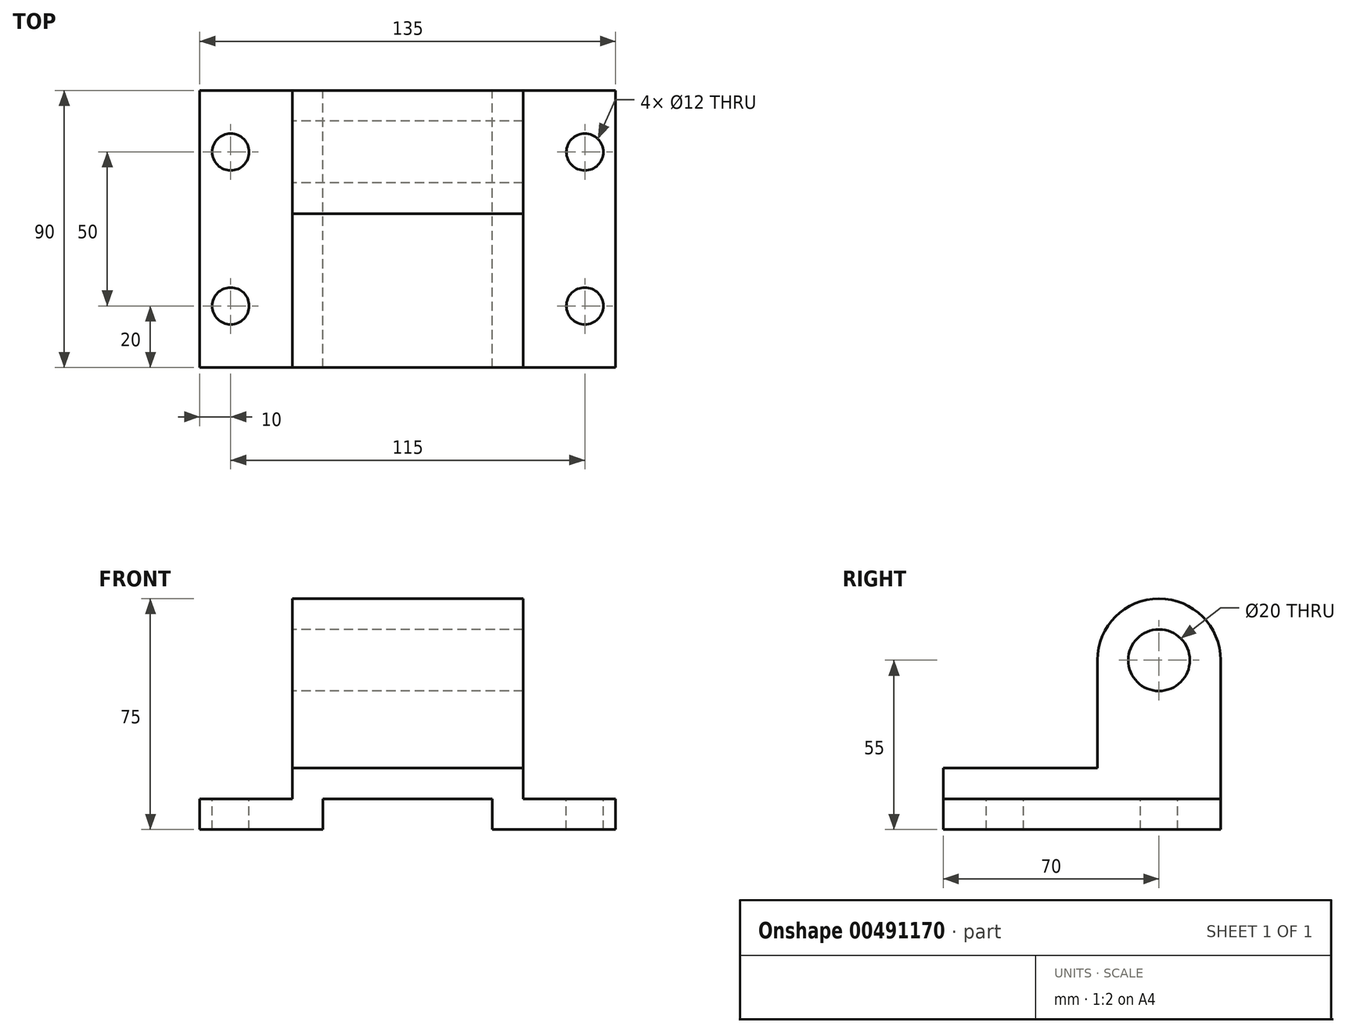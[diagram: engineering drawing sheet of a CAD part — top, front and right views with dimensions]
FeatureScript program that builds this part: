
annotation { "Feature Type Name" : "Feature", "Feature Type Description" : "" }
export const myFeature = defineFeature(function(context is Context, id is Id, definition is map)
    precondition{}
    {
        {
            var Q0;
            Q0=qCreatedBy(makeId("Front.planeOp"),FACE);
            var sketch = newSketch(context, id + "F0", { "sketchPlane" : qUnion([Q0])});
            skLineSegment(sketch, "E0", {"start": v(-95, 0) * mm, "end": v(-55, 0) * mm});
            skLineSegment(sketch, "E1", {"start": v(-55, 0) * mm, "end": v(-55, 10) * mm});
            skLineSegment(sketch, "E2", {"start": v(-55, 10) * mm, "end": v(0, 10) * mm});
            skLineSegment(sketch, "E3", {"start": v(0, 10) * mm, "end": v(0, 0) * mm});
            skLineSegment(sketch, "E4", {"start": v(0, 0) * mm, "end": v(40, 0) * mm});
            skLineSegment(sketch, "E5", {"start": v(40, 0) * mm, "end": v(40, 10) * mm});
            skLineSegment(sketch, "E6", {"start": v(40, 10) * mm, "end": v(10, 10) * mm});
            skLineSegment(sketch, "E7", {"start": v(10, 10) * mm, "end": v(10, 20) * mm});
            skLineSegment(sketch, "E8", {"start": v(10, 20) * mm, "end": v(-65, 20) * mm});
            skLineSegment(sketch, "E9", {"start": v(-65, 20) * mm, "end": v(-65, 10) * mm});
            skLineSegment(sketch, "E10", {"start": v(-65, 10) * mm, "end": v(-95, 10) * mm});
            skLineSegment(sketch, "E11", {"start": v(-95, 10) * mm, "end": v(-95, 0) * mm});
            skSolve(sketch);
        }
        {
            var Q0;
            Q0=makeQuery(id+"F0.imprint","IMPRINT",FACE,{"disambiguationData":[TD([[makeQuery(id+"F0.imprint","IMPRINT",EDGE,{"derivedFrom":sQuery(id+"F0.wireOp",EDGE,"E0")}),1.0]])]});
            extrude(context, id + "F1", {"entities" : qUnion([Q0]), "depth" : 90 * mm});
        }
        {
            var Q0;
            Q0=makeQuery(id+"F1.opExtrude","SWEPT_FACE",FACE,{"disambiguationData":[OSD([sQuery(id+"F0.wireOp",EDGE,"E10")])]});
            var sketch = newSketch(context, id + "F2", { "sketchPlane" : qUnion([Q0])});
            skCircle(sketch, "E12", {"center": v(-85, -70) * mm, "radius": 6 * mm});
            skSolve(sketch);
        }
        {
            var Q0;
            Q0=makeQuery(id+"F2.imprint","IMPRINT",FACE,{"disambiguationData":[TD([[makeQuery(id+"F2.imprint","IMPRINT",EDGE,{"derivedFrom":sQuery(id+"F2.wireOp",EDGE,"E12")}),1.0]])]});
            extrude(context, id + "F3", {"entities" : qUnion([Q0]), "operationType" : NewBodyOperationType.REMOVE, "oppositeDirection" : true, "depth" : 10 * mm});
        }
        {
            var Q0;
            Q0=makeQuery(id+"F1.opExtrude","SWEPT_FACE",FACE,{"disambiguationData":[OSD([sQuery(id+"F0.wireOp",EDGE,"E6")])]});
            var sketch = newSketch(context, id + "F4", { "sketchPlane" : qUnion([Q0])});
            skCircle(sketch, "E13", {"center": v(30, -70) * mm, "radius": 6 * mm});
            skSolve(sketch);
        }
        {
            var Q0;
            Q0=makeQuery(id+"F4.imprint","IMPRINT",FACE,{"disambiguationData":[TD([[makeQuery(id+"F4.imprint","IMPRINT",EDGE,{"derivedFrom":sQuery(id+"F4.wireOp",EDGE,"E13")}),1.0]])]});
            extrude(context, id + "F5", {"entities" : qUnion([Q0]), "operationType" : NewBodyOperationType.REMOVE, "oppositeDirection" : true, "depth" : 10 * mm});
        }
        {
            var Q0;
            Q0=makeQuery(id+"F1.opExtrude","SWEPT_FACE",FACE,{"disambiguationData":[OSD([sQuery(id+"F0.wireOp",EDGE,"E10")])]});
            var sketch = newSketch(context, id + "F6", { "sketchPlane" : qUnion([Q0])});
            skCircle(sketch, "E14", {"center": v(-85, -20) * mm, "radius": 6 * mm});
            skSolve(sketch);
        }
        {
            var Q0;
            Q0=makeQuery(id+"F1.opExtrude","SWEPT_FACE",FACE,{"disambiguationData":[OSD([sQuery(id+"F0.wireOp",EDGE,"E6")])]});
            var sketch = newSketch(context, id + "F7", { "sketchPlane" : qUnion([Q0])});
            skCircle(sketch, "E15", {"center": v(30, -20) * mm, "radius": 6 * mm});
            skSolve(sketch);
        }
        {
            var Q0;
            Q0=makeQuery(id+"F6.imprint","IMPRINT",FACE,{"disambiguationData":[TD([[makeQuery(id+"F6.imprint","IMPRINT",EDGE,{"derivedFrom":sQuery(id+"F6.wireOp",EDGE,"E14")}),1.0]])]});
            extrude(context, id + "F8", {"entities" : qUnion([Q0]), "operationType" : NewBodyOperationType.REMOVE, "oppositeDirection" : true, "depth" : 10 * mm});
        }
        {
            var Q0;
            Q0=makeQuery(id+"F7.imprint","IMPRINT",FACE,{"disambiguationData":[TD([[makeQuery(id+"F7.imprint","IMPRINT",EDGE,{"derivedFrom":sQuery(id+"F7.wireOp",EDGE,"E15")}),1.0]])]});
            extrude(context, id + "F9", {"entities" : qUnion([Q0]), "operationType" : NewBodyOperationType.REMOVE, "oppositeDirection" : true, "depth" : 10 * mm});
        }
        {
            var Q0;
            Q0=makeQuery(id+"F1.opExtrude","SWEPT_FACE",FACE,{"disambiguationData":[OSD([sQuery(id+"F0.wireOp",EDGE,"E9")])]});
            var sketch = newSketch(context, id + "F10", { "sketchPlane" : qUnion([Q0])});
            skLineSegment(sketch, "E16.bottom", {"start": v(0, 20) * mm, "end": v(40, 20) * mm});
            skLineSegment(sketch, "E16.left", {"start": v(0, 20) * mm, "end": v(0, 55) * mm});
            skLineSegment(sketch, "E16.right", {"start": v(40, 20) * mm, "end": v(40, 55) * mm});
            skArc(sketch, "E17", {"start": v(40, 55) * mm, "mid": v(20, 75) * mm, "end": v(0, 55) * mm});
            skCircle(sketch, "E18", {"center": v(20, 55) * mm, "radius": 10 * mm});
            skSolve(sketch);
        }
        {
            var Q0;
            Q0=makeQuery(id+"F10.imprint","IMPRINT",FACE,{"disambiguationData":[TD([[makeQuery(id+"F10.imprint","IMPRINT",EDGE,{"derivedFrom":sQuery(id+"F10.wireOp",EDGE,"E16.bottom")}),-1.0]])]});
            var Q1;
            Q1=makeQuery(id+"F1.opExtrude","SWEPT_FACE",FACE,{"disambiguationData":[OSD([sQuery(id+"F0.wireOp",EDGE,"E7")])]});
            extrude(context, id + "F11", {"entities" : qUnion([Q0]), "operationType" : NewBodyOperationType.ADD, "endBound" : BoundingType.UP_TO_SURFACE, "oppositeDirection" : true, "endBoundEntityFace" : qUnion([Q1]), "depth" : 25 * mm});
        }
    });
